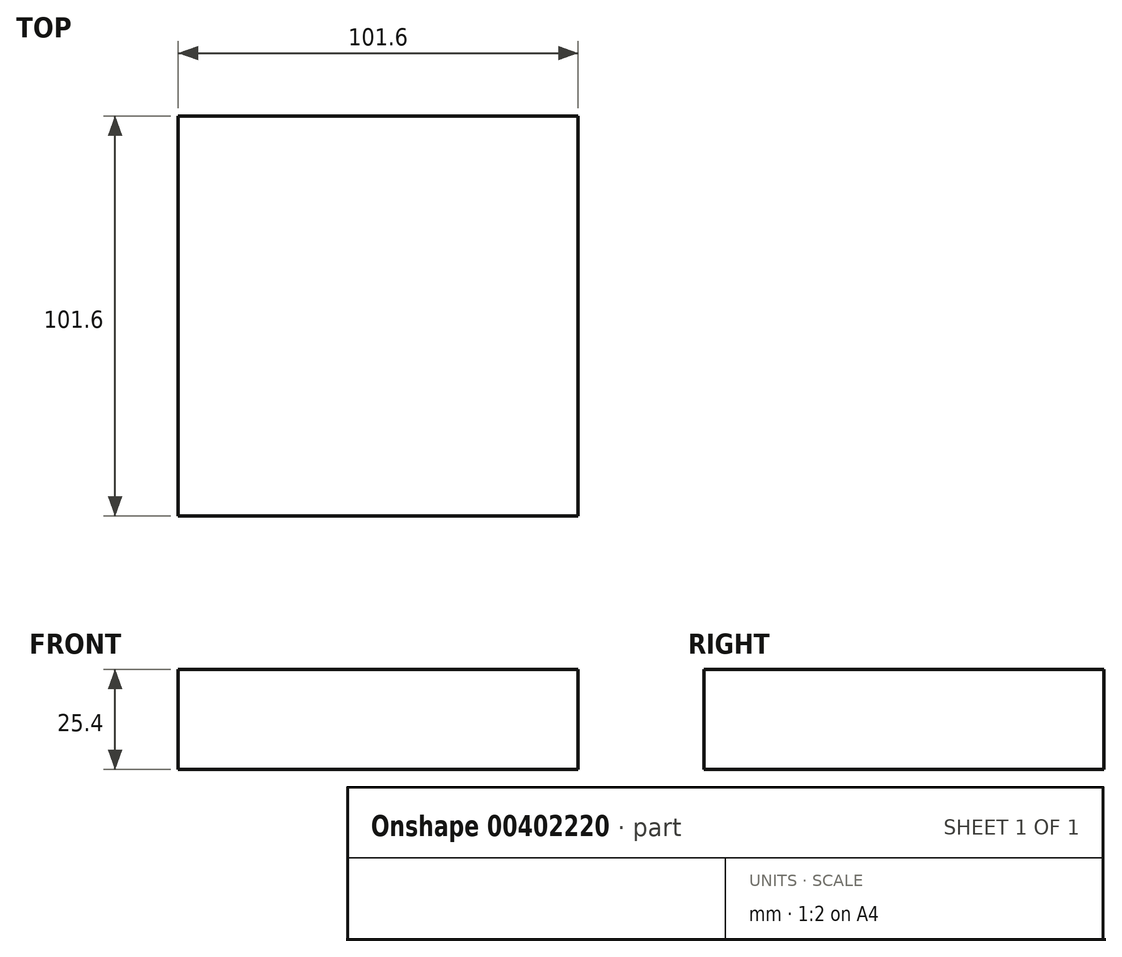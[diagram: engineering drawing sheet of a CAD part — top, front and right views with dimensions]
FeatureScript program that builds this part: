
annotation { "Feature Type Name" : "Feature", "Feature Type Description" : "" }
export const myFeature = defineFeature(function(context is Context, id is Id, definition is map)
    precondition{}
    {
        {
            var Q0;
            Q0=qCreatedBy(makeId("Top.planeOp"),FACE);
            var sketch = newSketch(context, id + "F0", { "sketchPlane" : qUnion([Q0])});
            skLineSegment(sketch, "E0.bottom", {"start": v(0, 0) * mm, "end": v(101.6, 0) * mm});
            skLineSegment(sketch, "E0.top", {"start": v(0, 101.6) * mm, "end": v(101.6, 101.6) * mm});
            skLineSegment(sketch, "E0.left", {"start": v(0, 0) * mm, "end": v(0, 101.6) * mm});
            skLineSegment(sketch, "E0.right", {"start": v(101.6, 0) * mm, "end": v(101.6, 101.6) * mm});
            skSolve(sketch);
        }
        {
            var Q0;
            Q0=makeQuery(id+"F0.imprint","IMPRINT",FACE,{"disambiguationData":[TD([[makeQuery(id+"F0.imprint","IMPRINT",EDGE,{"derivedFrom":sQuery(id+"F0.wireOp",EDGE,"E0.bottom")}),1.0]])]});
            extrude(context, id + "F1", {"entities" : qUnion([Q0]), "depth" : 25.4 * mm});
        }
    });
